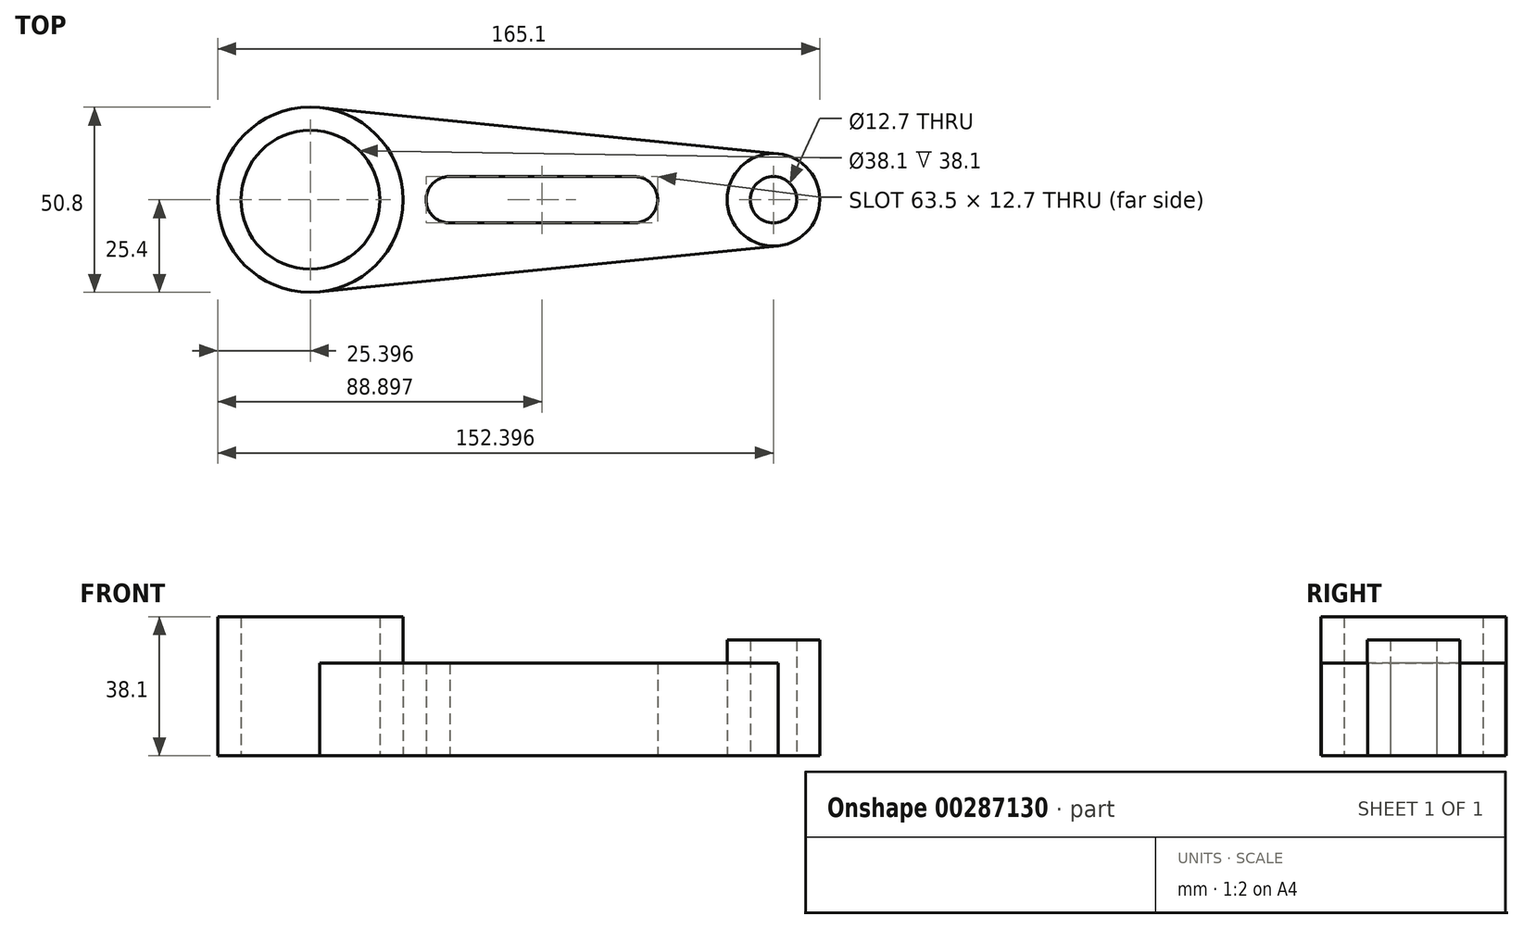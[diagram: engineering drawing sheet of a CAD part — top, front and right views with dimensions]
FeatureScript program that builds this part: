
annotation { "Feature Type Name" : "Feature", "Feature Type Description" : "" }
export const myFeature = defineFeature(function(context is Context, id is Id, definition is map)
    precondition{}
    {
        {
            var Q0;
            Q0=qCreatedBy(makeId("Top.planeOp"),FACE);
            var sketch = newSketch(context, id + "F0", { "sketchPlane" : qUnion([Q0])});
            skCircle(sketch, "E0", {"center": v(-45.5, 0) * mm, "radius": 19.05 * mm});
            skCircle(sketch, "E1", {"center": v(-45.5, 0) * mm, "radius": 25.4 * mm});
            skCircle(sketch, "E2", {"center": v(81.5, 0) * mm, "radius": 12.7 * mm});
            skArc(sketch, "E3", {"start": v(-7.2, 6.35) * mm, "mid": v(-13.74, 0.1) * mm, "end": v(-7.4, -6.35) * mm});
            skArc(sketch, "E4", {"start": v(43.4, -6.35) * mm, "mid": v(49.76, 0) * mm, "end": v(43.4, 6.35) * mm});
            skLineSegment(sketch, "E5", {"start": v(-7.2, 6.35) * mm, "end": v(43.4, 6.35) * mm});
            skLineSegment(sketch, "E6", {"start": v(-7.4, -6.35) * mm, "end": v(43.4, -6.35) * mm});
            skCircle(sketch, "E7", {"center": v(81.5, 0) * mm, "radius": 6.35 * mm});
            skLineSegment(sketch, "E8", {"start": v(-42.95, -25.27) * mm, "end": v(82.78, -12.64) * mm});
            skLineSegment(sketch, "E9", {"start": v(82.78, 12.64) * mm, "end": v(-42.95, 25.27) * mm});
            skSolve(sketch);
        }
        {
            var Q0;
            Q0=makeQuery(id+"F0.imprint","IMPRINT",FACE,{"disambiguationData":[TD([[makeQuery(id+"F0.imprint","IMPRINT",EDGE,{"derivedFrom":sQuery(id+"F0.wireOp",EDGE,"E0")}),-1.0]])]});
            extrude(context, id + "F1", {"entities" : qUnion([Q0]), "depth" : 38.1 * mm});
        }
        {
            var Q0;
            Q0=makeQuery(id+"F0.imprint","IMPRINT",FACE,{"disambiguationData":[TD([[makeQuery(id+"F0.imprint","IMPRINT",EDGE,{"derivedFrom":sQuery(id+"F0.wireOp",EDGE,"E7")}),-1.0]])]});
            extrude(context, id + "F2", {"entities" : qUnion([Q0]), "depth" : 31.75 * mm});
        }
        {
            var Q0;
            {var subQ3=sQuery(id+"F0.wireOp",EDGE,"E6");Q0=makeQuery(id+"F0.imprint","IMPRINT",FACE,{"disambiguationData":[TD([[makeQuery(id+"F0.imprint","IMPRINT",EDGE,{"derivedFrom":subQ3}),-1.0]])]});}
            extrude(context, id + "F3", {"entities" : qUnion([Q0]), "depth" : 25.4 * mm});
        }
    });
